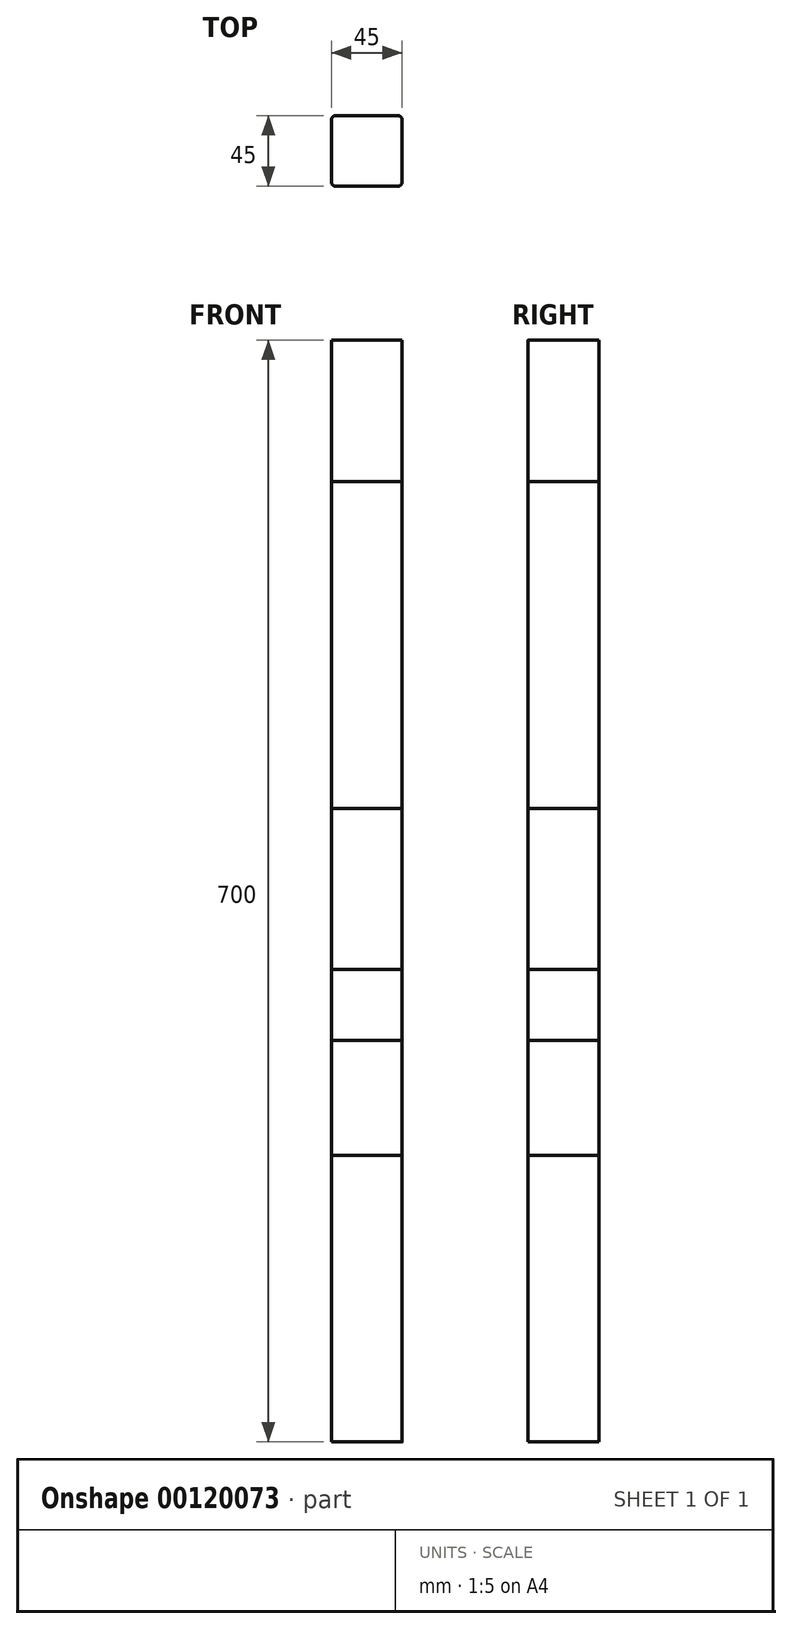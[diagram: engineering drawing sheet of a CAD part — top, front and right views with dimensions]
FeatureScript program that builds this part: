
annotation { "Feature Type Name" : "Feature", "Feature Type Description" : "" }
export const myFeature = defineFeature(function(context is Context, id is Id, definition is map)
    precondition{}
    {
        {
            var Q0;
            Q0=qCreatedBy(makeId("Top.planeOp"),FACE);
            var sketch = newSketch(context, id + "F0", { "sketchPlane" : qUnion([Q0])});
            skLineSegment(sketch, "E0.bottom", {"start": v(19.5, 22.5) * mm, "end": v(-19.5, 22.5) * mm});
            skLineSegment(sketch, "E0.top", {"start": v(19.5, -22.5) * mm, "end": v(-19.5, -22.5) * mm});
            skLineSegment(sketch, "E0.left", {"start": v(22.5, 19.5) * mm, "end": v(22.5, -19.5) * mm});
            skLineSegment(sketch, "E0.right", {"start": v(-22.5, 19.5) * mm, "end": v(-22.5, -19.5) * mm});
            skPoint(sketch, "E0.middle", {"position": v(0, 0) * mm});
            skPoint(sketch, "E1.visualSharp", {"position": v(-22.5, 22.5) * mm});
            skArc(sketch, "E1.filletArc", {"start": v(-19.5, 22.5) * mm, "mid": v(-21.62, 21.62) * mm, "end": v(-22.5, 19.5) * mm});
            skPoint(sketch, "E2.visualSharp", {"position": v(22.5, 22.5) * mm});
            skArc(sketch, "E2.filletArc", {"start": v(22.5, 19.5) * mm, "mid": v(21.62, 21.62) * mm, "end": v(19.5, 22.5) * mm});
            skPoint(sketch, "E3.visualSharp", {"position": v(22.5, -22.5) * mm});
            skArc(sketch, "E3.filletArc", {"start": v(19.5, -22.5) * mm, "mid": v(21.62, -21.62) * mm, "end": v(22.5, -19.5) * mm});
            skPoint(sketch, "E4.visualSharp", {"position": v(-22.5, -22.5) * mm});
            skArc(sketch, "E4.filletArc", {"start": v(-22.5, -19.5) * mm, "mid": v(-21.62, -21.62) * mm, "end": v(-19.5, -22.5) * mm});
            skSolve(sketch);
        }
        {
            var Q0;
            Q0 = qSketchRegion(id + "F0", true);
            extrude(context, id + "F1", {"entities" : qUnion([Q0]), "depth" : 610 * mm});
        }
        {
            var Q0;
            Q0 = qSketchRegion(id + "F0", true);
            extrude(context, id + "F2", {"entities" : qUnion([Q0]), "depth" : 700 * mm});
        }
        {
            var Q0;
            Q0 = qSketchRegion(id + "F0", true);
            extrude(context, id + "F3", {"entities" : qUnion([Q0]), "depth" : 300 * mm});
        }
        {
            var Q0;
            Q0 = qSketchRegion(id + "F0", true);
            extrude(context, id + "F4", {"entities" : qUnion([Q0]), "depth" : 255 * mm});
        }
        {
            var Q0;
            Q0 = qSketchRegion(id + "F0", true);
            extrude(context, id + "F5", {"entities" : qUnion([Q0]), "depth" : 182 * mm});
        }
        {
            var Q0;
            Q0 = qSketchRegion(id + "F0", true);
            extrude(context, id + "F6", {"entities" : qUnion([Q0]), "depth" : 402.5 * mm});
        }
    });
